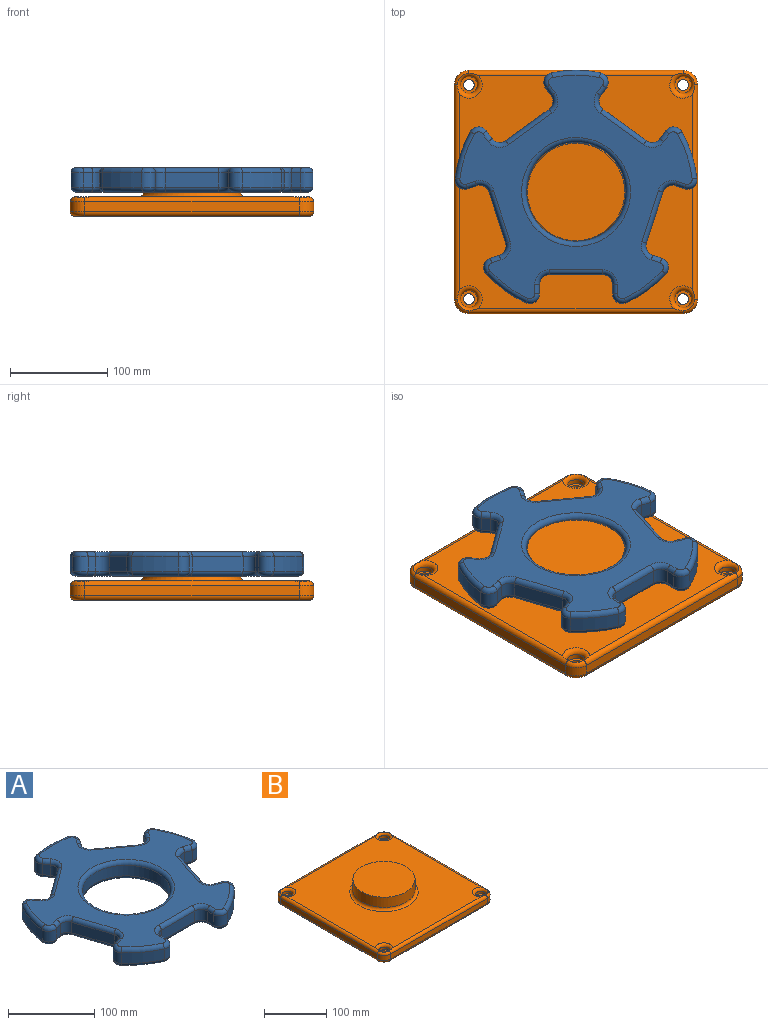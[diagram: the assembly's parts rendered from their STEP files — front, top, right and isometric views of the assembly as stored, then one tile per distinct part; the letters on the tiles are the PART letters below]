
ASSEMBLY  parts=2 mates=1
PART A: 125 faces, bbox 268.9x258.5x25 mm
  f0: plane 238.57x229.73mm, normal (0,0,1), area 19825mm2, adj f83,f84,f85,f86,f87,f88,f89,f90
  f1: plane 238.57x229.73mm, normal (0,0,-1), area 19825mm2, adj f43,f44,f45,f46,f47,f48,f49,f50
  f2: cylinder r=125mm len=47.82mm, axis (0,0,-1), area 759.5mm2, adj f34,f42,f72,f113
  f3: cylinder r=125mm len=50.29mm, axis (0,0,-1), area 759.5mm2, adj f27,f35,f56,f97
  f4: cylinder r=125mm len=47.82mm, axis (0,0,-1), area 759.5mm2, adj f20,f28,f45,f84
  f5: cylinder r=125mm len=40.68mm, axis (0,0,-1), area 759.5mm2, adj f13,f21,f61,f100
  f6: cylinder r=51mm len=102mm, axis (0,0,-1), area 4806.6mm2, adj f123,f124
  f7: cylinder r=125mm len=40.68mm, axis (0,0,-1), area 759.5mm2, adj f14,f41,f77,f116
  f8: plane 15x9.73mm, normal (-1,0,0), area 146mm2, adj f11,f14,f73,f112
  f9: plane 55x15mm, normal (0,-1,0), area 825mm2, adj f11,f12,f69,f108
  f10: plane 15x9.73mm, normal (1,0,0), area 146mm2, adj f12,f13,f65,f104
  f11: cylinder r=10mm len=15mm, axis (0,0,-1), area 235.6mm2, adj f8,f9,f71,f110
  f12: cylinder r=10mm len=15mm, axis (0,0,-1), area 235.6mm2, adj f9,f10,f67,f106
  f13: cylinder r=10mm len=15mm, axis (0,0,-1), area 299.5mm2, adj f5,f10,f63,f102
  f14: cylinder r=10mm len=15mm, axis (0,0,-1), area 299.5mm2, adj f7,f8,f75,f114
  f15: plane 15x9.26mm, normal (-0.31,0.95,0), area 146mm2, adj f18,f21,f57,f96
  f16: plane 52.31x17mm, normal (-0.95,-0.31,0), area 825mm2, adj f18,f19,f53,f92
  f17: plane 15x9.26mm, normal (0.31,-0.95,0), area 146mm2, adj f19,f20,f49,f88
  f18: cylinder r=10mm len=15mm, axis (0,0,-1), area 235.6mm2, adj f15,f16,f55,f94
  f19: cylinder r=10mm len=15mm, axis (0,0,-1), area 235.6mm2, adj f16,f17,f51,f90
  f20: cylinder r=10mm len=15mm, axis (0,0,-1), area 299.5mm2, adj f4,f17,f47,f86
  f21: cylinder r=10mm len=16.25mm, axis (0,0,-1), area 299.5mm2, adj f5,f15,f59,f98
  f22: plane 15x7.87mm, normal (0.81,0.59,0), area 146mm2, adj f25,f28,f44,f85
  f23: plane 44.5x32.33mm, normal (-0.59,0.81,0), area 825mm2, adj f25,f26,f48,f89
  f24: plane 15x7.87mm, normal (-0.81,-0.59,0), area 146mm2, adj f26,f27,f52,f93
  f25: cylinder r=10mm len=15mm, axis (0,0,-1), area 235.6mm2, adj f22,f23,f46,f87
  f26: cylinder r=10mm len=15mm, axis (0,0,-1), area 235.6mm2, adj f23,f24,f50,f91
  f27: cylinder r=10mm len=15.67mm, axis (0,0,-1), area 299.5mm2, adj f3,f24,f54,f95
  f28: cylinder r=10mm len=16.78mm, axis (0,0,-1), area 299.5mm2, adj f4,f22,f43,f83
  f29: plane 15x7.87mm, normal (0.81,-0.59,0), area 146mm2, adj f32,f35,f60,f101
  f30: plane 44.5x32.33mm, normal (0.59,0.81,0), area 825mm2, adj f32,f33,f64,f105
  f31: plane 15x7.87mm, normal (-0.81,0.59,0), area 146mm2, adj f33,f34,f68,f109
  f32: cylinder r=10mm len=15mm, axis (0,0,-1), area 235.6mm2, adj f29,f30,f62,f103
  f33: cylinder r=10mm len=15mm, axis (0,0,-1), area 235.6mm2, adj f30,f31,f66,f107
  f34: cylinder r=10mm len=16.78mm, axis (0,0,-1), area 299.5mm2, adj f2,f31,f70,f111
  f35: cylinder r=10mm len=15.67mm, axis (0,0,-1), area 299.5mm2, adj f3,f29,f58,f99
  f36: plane 15x9.26mm, normal (-0.31,-0.95,0), area 146mm2, adj f39,f42,f76,f117
  f37: plane 52.31x17mm, normal (0.95,-0.31,0), area 825mm2, adj f39,f40,f80,f121
  f38: plane 15x9.26mm, normal (0.31,0.95,0), area 146mm2, adj f40,f41,f81,f120
  f39: cylinder r=10mm len=15mm, axis (0,0,-1), area 235.6mm2, adj f36,f37,f78,f119
  f40: cylinder r=10mm len=15mm, axis (0,0,-1), area 235.6mm2, adj f37,f38,f82,f122
  f41: cylinder r=10mm len=16.25mm, axis (0,0,-1), area 299.5mm2, adj f7,f38,f79,f118
  f42: cylinder r=10mm len=15mm, axis (0,0,-1), area 299.5mm2, adj f2,f36,f74,f115
  f43: torus R=5mm, axis (0,0,1), area 128.3mm2, adj f1,f28,f44,f45
  f44: cylinder r=5mm len=10.81mm, axis (0.59,-0.81,0), area 76.4mm2, adj f1,f22,f43,f46
  f45: torus R=120mm, axis (0,0,1), area 391.9mm2, adj f1,f4,f43,f47
  f46: torus R=15mm, axis (0,0,1), area 145.8mm2, adj f1,f25,f44,f48
  f47: torus R=5mm, axis (0,0,1), area 128.3mm2, adj f1,f20,f45,f49
  f48: cylinder r=5mm len=47.44mm, axis (0.81,0.59,0), area 432mm2, adj f1,f23,f46,f50
  f49: cylinder r=5mm len=10.8mm, axis (-0.95,-0.31,0), area 76.4mm2, adj f1,f17,f47,f51
  f50: torus R=15mm, axis (0,0,1), area 145.8mm2, adj f1,f26,f48,f52
  f51: torus R=15mm, axis (0,0,1), area 145.8mm2, adj f1,f19,f49,f53
  f52: cylinder r=5mm len=10.81mm, axis (-0.59,0.81,0), area 76.4mm2, adj f1,f24,f50,f54
  f53: cylinder r=5mm len=53.85mm, axis (-0.31,0.95,0), area 432mm2, adj f1,f16,f51,f55
  f54: torus R=5mm, axis (0,0,1), area 128.3mm2, adj f1,f27,f52,f56
  f55: torus R=15mm, axis (0,0,1), area 145.8mm2, adj f1,f18,f53,f57
  f56: torus R=120mm, axis (0,0,1), area 391.9mm2, adj f1,f3,f54,f58
  f57: cylinder r=5mm len=10.8mm, axis (0.95,0.31,0), area 76.4mm2, adj f1,f15,f55,f59
  f58: torus R=5mm, axis (0,0,1), area 128.3mm2, adj f1,f35,f56,f60
  f59: torus R=5mm, axis (0,0,1), area 128.3mm2, adj f1,f21,f57,f61
  f60: cylinder r=5mm len=10.81mm, axis (-0.59,-0.81,0), area 76.4mm2, adj f1,f29,f58,f62
  f61: torus R=120mm, axis (0,0,1), area 391.9mm2, adj f1,f5,f59,f63
  f62: torus R=15mm, axis (0,0,1), area 145.8mm2, adj f1,f32,f60,f64
  f63: torus R=5mm, axis (0,0,1), area 128.3mm2, adj f1,f13,f61,f65
  f64: cylinder r=5mm len=47.44mm, axis (0.81,-0.59,0), area 432mm2, adj f1,f30,f62,f66
  f65: cylinder r=5mm len=9.73mm, axis (0,-1,0), area 76.4mm2, adj f1,f10,f63,f67
  f66: torus R=15mm, axis (0,0,1), area 145.8mm2, adj f1,f33,f64,f68
  f67: torus R=15mm, axis (0,0,1), area 145.8mm2, adj f1,f12,f65,f69
  f68: cylinder r=5mm len=10.81mm, axis (0.59,0.81,0), area 76.4mm2, adj f1,f31,f66,f70
  f69: cylinder r=5mm len=55mm, axis (-1,0,0), area 432mm2, adj f1,f9,f67,f71
  f70: torus R=5mm, axis (0,0,1), area 128.3mm2, adj f1,f34,f68,f72
  f71: torus R=15mm, axis (0,0,1), area 145.8mm2, adj f1,f11,f69,f73
  f72: torus R=120mm, axis (0,0,1), area 391.9mm2, adj f1,f2,f70,f74
  f73: cylinder r=5mm len=9.73mm, axis (0,1,0), area 76.4mm2, adj f1,f8,f71,f75
  f74: torus R=5mm, axis (0,0,1), area 128.3mm2, adj f1,f42,f72,f76
  f75: torus R=5mm, axis (0,0,1), area 128.3mm2, adj f1,f14,f73,f77
  f76: cylinder r=5mm len=10.8mm, axis (-0.95,0.31,0), area 76.4mm2, adj f1,f36,f74,f78
  f77: torus R=120mm, axis (0,0,1), area 391.9mm2, adj f1,f7,f75,f79
  f78: torus R=15mm, axis (0,0,1), area 145.8mm2, adj f1,f39,f76,f80
  f79: torus R=5mm, axis (0,0,1), area 128.3mm2, adj f1,f41,f77,f81
  f80: cylinder r=5mm len=53.85mm, axis (-0.31,-0.95,0), area 432mm2, adj f1,f37,f78,f82
  f81: cylinder r=5mm len=10.8mm, axis (0.95,-0.31,0), area 76.4mm2, adj f1,f38,f79,f82
  f82: torus R=15mm, axis (0,0,1), area 145.8mm2, adj f1,f40,f80,f81
  f83: torus R=5mm, axis (0,0,1), area 128.3mm2, adj f0,f28,f84,f85
  f84: torus R=120mm, axis (0,0,1), area 391.9mm2, adj f0,f4,f83,f86
  f85: cylinder r=5mm len=10.81mm, axis (-0.59,0.81,0), area 76.4mm2, adj f0,f22,f83,f87
  f86: torus R=5mm, axis (0,0,1), area 128.3mm2, adj f0,f20,f84,f88
  f87: torus R=15mm, axis (0,0,1), area 145.8mm2, adj f0,f25,f85,f89
  f88: cylinder r=5mm len=10.8mm, axis (0.95,0.31,0), area 76.4mm2, adj f0,f17,f86,f90
  f89: cylinder r=5mm len=47.44mm, axis (-0.81,-0.59,0), area 432mm2, adj f0,f23,f87,f91
  f90: torus R=15mm, axis (0,0,1), area 145.8mm2, adj f0,f19,f88,f92
  f91: torus R=15mm, axis (0,0,1), area 145.8mm2, adj f0,f26,f89,f93
  f92: cylinder r=5mm len=53.85mm, axis (0.31,-0.95,0), area 432mm2, adj f0,f16,f90,f94
  f93: cylinder r=5mm len=10.81mm, axis (0.59,-0.81,0), area 76.4mm2, adj f0,f24,f91,f95
  f94: torus R=15mm, axis (0,0,1), area 145.8mm2, adj f0,f18,f92,f96
  f95: torus R=5mm, axis (0,0,1), area 128.3mm2, adj f0,f27,f93,f97
  f96: cylinder r=5mm len=10.8mm, axis (-0.95,-0.31,0), area 76.4mm2, adj f0,f15,f94,f98
  f97: torus R=120mm, axis (0,0,1), area 391.9mm2, adj f0,f3,f95,f99
  f98: torus R=5mm, axis (0,0,1), area 128.3mm2, adj f0,f21,f96,f100
  f99: torus R=5mm, axis (0,0,1), area 128.3mm2, adj f0,f35,f97,f101
  f100: torus R=120mm, axis (0,0,1), area 391.9mm2, adj f0,f5,f98,f102
  f101: cylinder r=5mm len=10.81mm, axis (0.59,0.81,0), area 76.4mm2, adj f0,f29,f99,f103
  f102: torus R=5mm, axis (0,0,1), area 128.3mm2, adj f0,f13,f100,f104
  f103: torus R=15mm, axis (0,0,1), area 145.8mm2, adj f0,f32,f101,f105
  f104: cylinder r=5mm len=9.73mm, axis (0,1,0), area 76.4mm2, adj f0,f10,f102,f106
  f105: cylinder r=5mm len=47.44mm, axis (-0.81,0.59,0), area 432mm2, adj f0,f30,f103,f107
  f106: torus R=15mm, axis (0,0,1), area 145.8mm2, adj f0,f12,f104,f108
  f107: torus R=15mm, axis (0,0,1), area 145.8mm2, adj f0,f33,f105,f109
  f108: cylinder r=5mm len=55mm, axis (1,0,0), area 432mm2, adj f0,f9,f106,f110
  f109: cylinder r=5mm len=10.81mm, axis (-0.59,-0.81,0), area 76.4mm2, adj f0,f31,f107,f111
  f110: torus R=15mm, axis (0,0,1), area 145.8mm2, adj f0,f11,f108,f112
  f111: torus R=5mm, axis (0,0,1), area 128.3mm2, adj f0,f34,f109,f113
  f112: cylinder r=5mm len=9.73mm, axis (0,-1,0), area 76.4mm2, adj f0,f8,f110,f114
  f113: torus R=120mm, axis (0,0,1), area 391.9mm2, adj f0,f2,f111,f115
  f114: torus R=5mm, axis (0,0,1), area 128.3mm2, adj f0,f14,f112,f116
  f115: torus R=5mm, axis (0,0,1), area 128.3mm2, adj f0,f42,f113,f117
  f116: torus R=120mm, axis (0,0,1), area 391.9mm2, adj f0,f7,f114,f118
  f117: cylinder r=5mm len=10.8mm, axis (0.95,-0.31,0), area 76.4mm2, adj f0,f36,f115,f119
  f118: torus R=5mm, axis (0,0,1), area 128.3mm2, adj f0,f41,f116,f120
  f119: torus R=15mm, axis (0,0,1), area 145.8mm2, adj f0,f39,f117,f121
  f120: cylinder r=5mm len=10.8mm, axis (-0.95,0.31,0), area 76.4mm2, adj f0,f38,f118,f122
  f121: cylinder r=5mm len=53.85mm, axis (0.31,0.95,0), area 432mm2, adj f0,f37,f119,f122
  f122: torus R=15mm, axis (0,0,1), area 145.8mm2, adj f0,f40,f120,f121
  f123: torus R=56mm, axis (0,0,1), area 2606.4mm2, adj f0,f6
  f124: torus R=56mm, axis (0,0,1), area 2606.4mm2, adj f1,f6
PART B: 49 faces, bbox 254.8x254.8x45 mm
  f0: plane 220x10mm, normal (1,0,0), area 2200mm2, adj f8,f11,f27,f44
  f1: plane 220x10mm, normal (0,1,0), area 2200mm2, adj f8,f9,f26,f38
  f2: plane 220x10mm, normal (-1,0,0), area 2200mm2, adj f9,f10,f32,f39
  f3: plane 220x10mm, normal (0,-1,0), area 2200mm2, adj f10,f11,f34,f46
  f4: plane 240x240mm, normal (0,0,1), area 46131.4mm2, adj f37,f38,f39,f40,f43,f44,f46,f47
  f5: plane 240x240mm, normal (0,0,-1), area 56169.5mm2, adj f25,f26,f27,f28,f31,f32,f34,f35
  f6: cylinder r=50mm len=100mm, axis (0,0,-1), area 6283.2mm2, adj f7,f48
  f7: plane 100x100mm, normal (0,0,1), area 7854mm2, adj f6
  f8: cylinder r=15mm len=15mm, axis (0,0,-1), area 235.6mm2, adj f0,f1,f24,f41
  f9: cylinder r=15mm len=15mm, axis (0,0,1), area 235.6mm2, adj f1,f2,f29,f36
  f10: cylinder r=15mm len=15mm, axis (0,0,-1), area 235.6mm2, adj f2,f3,f33,f42
  f11: cylinder r=15mm len=15mm, axis (0,0,1), area 235.6mm2, adj f0,f3,f30,f45
  f12: cylinder r=5.5mm len=11mm, axis (0,0,1), area 172.8mm2, adj f13,f28
  f13: plane 17.25x17.25mm, normal (0,0,1), area 138.7mm2, adj f12,f14
  f14: cylinder r=8.62mm len=17.25mm, axis (0,0,1), area 271mm2, adj f13,f37
  f15: cylinder r=5.5mm len=11mm, axis (0,0,1), area 172.8mm2, adj f16,f31
  f16: plane 17.25x17.25mm, normal (0,0,1), area 138.7mm2, adj f15,f17
  f17: cylinder r=8.62mm len=17.25mm, axis (0,0,1), area 271mm2, adj f16,f47
  f18: cylinder r=5.5mm len=11mm, axis (0,0,1), area 172.8mm2, adj f19,f25
  f19: plane 17.25x17.25mm, normal (0,0,1), area 138.7mm2, adj f18,f20
  f20: cylinder r=8.62mm len=17.25mm, axis (0,0,1), area 271mm2, adj f19,f40
  f21: cylinder r=5.5mm len=11mm, axis (0,0,1), area 172.8mm2, adj f22,f35
  f22: plane 17.25x17.25mm, normal (0,0,1), area 138.7mm2, adj f21,f23
  f23: cylinder r=8.62mm len=17.25mm, axis (0,0,1), area 271mm2, adj f22,f43
  f24: torus R=10mm, axis (0,0,1), area 158.7mm2, adj f8,f25,f26,f27
  f25: torus R=10.5mm, axis (0,0,1), area 356.2mm2, adj f5,f18,f24,f26,f27
  f26: cylinder r=5mm len=220mm, axis (-1,0,0), area 1727.1mm2, adj f1,f5,f24,f25,f28,f29
  f27: cylinder r=5mm len=220mm, axis (0,1,0), area 1727.1mm2, adj f0,f5,f24,f25,f30,f31
  f28: torus R=10.5mm, axis (0,0,1), area 356.2mm2, adj f5,f12,f26,f29,f32
  f29: torus R=10mm, axis (0,0,1), area 158.7mm2, adj f9,f26,f28,f32
  f30: torus R=10mm, axis (0,0,1), area 158.7mm2, adj f11,f27,f31,f34
  f31: torus R=10.5mm, axis (0,0,1), area 356.2mm2, adj f5,f15,f27,f30,f34
  f32: cylinder r=5mm len=220mm, axis (0,-1,0), area 1727.1mm2, adj f2,f5,f28,f29,f33,f35
  f33: torus R=10mm, axis (0,0,1), area 158.7mm2, adj f10,f32,f34,f35
  f34: cylinder r=5mm len=220mm, axis (1,0,0), area 1727.1mm2, adj f3,f5,f30,f31,f33,f35
  f35: torus R=10.5mm, axis (0,0,1), area 356.2mm2, adj f5,f21,f32,f33,f34
  f36: torus R=10mm, axis (0,0,1), area 130.8mm2, adj f9,f37,f38,f39
  f37: torus R=13.62mm, axis (0,0,1), area 454.2mm2, adj f4,f14,f36,f38,f39
  f38: cylinder r=5mm len=220mm, axis (1,0,0), area 1705.2mm2, adj f1,f4,f36,f37,f40,f41
  f39: cylinder r=5mm len=220mm, axis (0,1,0), area 1705.2mm2, adj f2,f4,f36,f37,f42,f43
  f40: torus R=13.62mm, axis (0,0,1), area 454.2mm2, adj f4,f20,f38,f41,f44
  f41: torus R=10mm, axis (0,0,1), area 130.8mm2, adj f8,f38,f40,f44
  f42: torus R=10mm, axis (0,0,1), area 130.8mm2, adj f10,f39,f43,f46
  f43: torus R=13.62mm, axis (0,0,1), area 454.2mm2, adj f4,f23,f39,f42,f46
  f44: cylinder r=5mm len=220mm, axis (0,-1,0), area 1705.2mm2, adj f0,f4,f40,f41,f45,f47
  f45: torus R=10mm, axis (0,0,1), area 130.8mm2, adj f11,f44,f46,f47
  f46: cylinder r=5mm len=220mm, axis (-1,0,0), area 1705.2mm2, adj f3,f4,f42,f43,f45,f47
  f47: torus R=13.62mm, axis (0,0,1), area 454.2mm2, adj f4,f17,f44,f45,f46
  f48: torus R=55mm, axis (0,0,1), area 2557.1mm2, adj f4,f6
PLACE A t=(279.7,-61.86,-48.46)mm
PLACE B t=(279.7,-61.86,-53.46)mm fixed
MATE revolute B.f6 <-> A.f2  axis (0,0,1) through (279.7,-61.86,-8.46)mm
